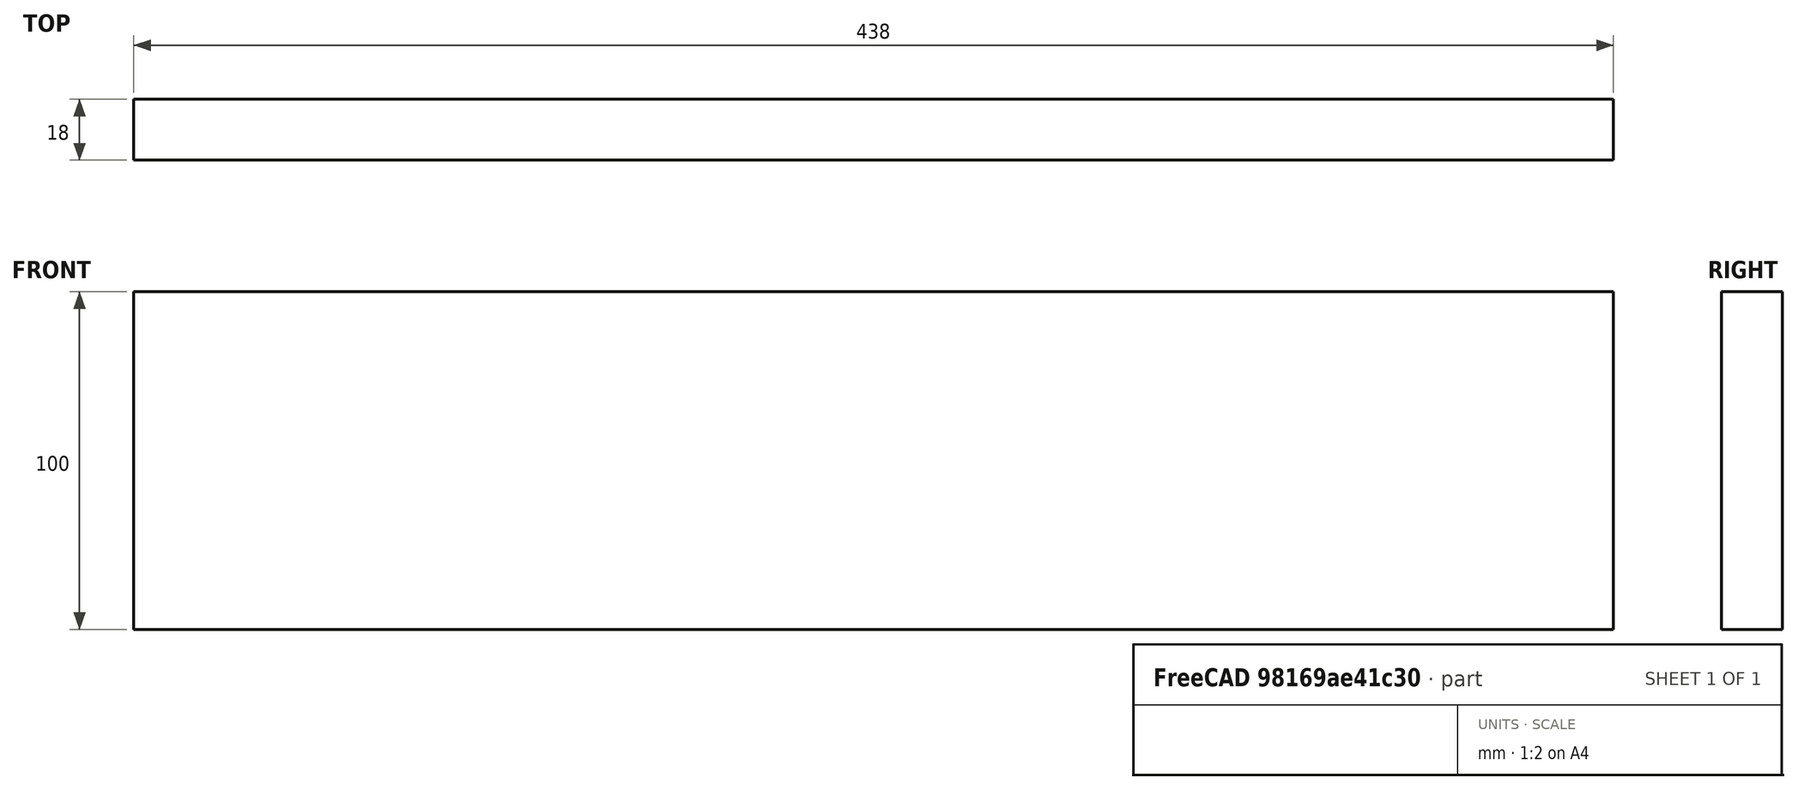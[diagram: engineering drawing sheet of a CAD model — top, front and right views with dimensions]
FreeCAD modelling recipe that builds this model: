
FCSTD DOCUMENT  (FreeCAD 0.18R4 (GitTag))
Label: drawer_back
License: All rights reserved
LicenseURL: http://en.wikipedia.org/wiki/All_rights_reserved
objects: Sketcher::SketchObject×1, PartDesign::Pad×1, PartDesign::Body×1
note: 4 computed .brp shape members not serialized (recipe doc carries the construction recipe); baked Part::Feature solids carry a one-line shape summary decoded from their .brp

FEATURE [Sketcher::SketchObject] Sketch
  MapMode = 5
  Placement = pos=(0,0,0) rot=(1,0,0;1.5708rad)
  Support = -> [XZ_Plane]
  sketch-geometry (4):
    g0: LineSegment StartX=0 StartY=0 StartZ=0 EndX=-438 EndY=0 EndZ=0
    g1: LineSegment StartX=-438 StartY=0 StartZ=0 EndX=-438 EndY=100 EndZ=0
    g2: LineSegment StartX=-438 StartY=100 StartZ=0 EndX=0 EndY=100 EndZ=0
    g3: LineSegment StartX=0 StartY=100 StartZ=0 EndX=0 EndY=0 EndZ=0
  constraints (11):
    c: Coincident(g0,g1)
    c: Coincident(g1,g2)
    c: Coincident(g2,g3)
    c: Coincident(g3,g0)
    c: Horizontal(g0)
    c: Horizontal(g2)
    c: Vertical(g1)
    c: Vertical(g3)
    c: Coincident(g0,g-1)
    c: DistanceX(g0,g0) = 438
    c: DistanceY(g3,g3) = 100
FEATURE [PartDesign::Pad] Pad
  Length = 18
  Length2 = 100
  Placement = pos=(0,0,0) rot=(1,0,0;1.5708rad)
  Profile = -> Sketch
  Type = 0
FEATURE [PartDesign::Body] Body
  Group = -> [Sketch,Pad]
  Origin = -> Origin
  Tip = -> Pad
